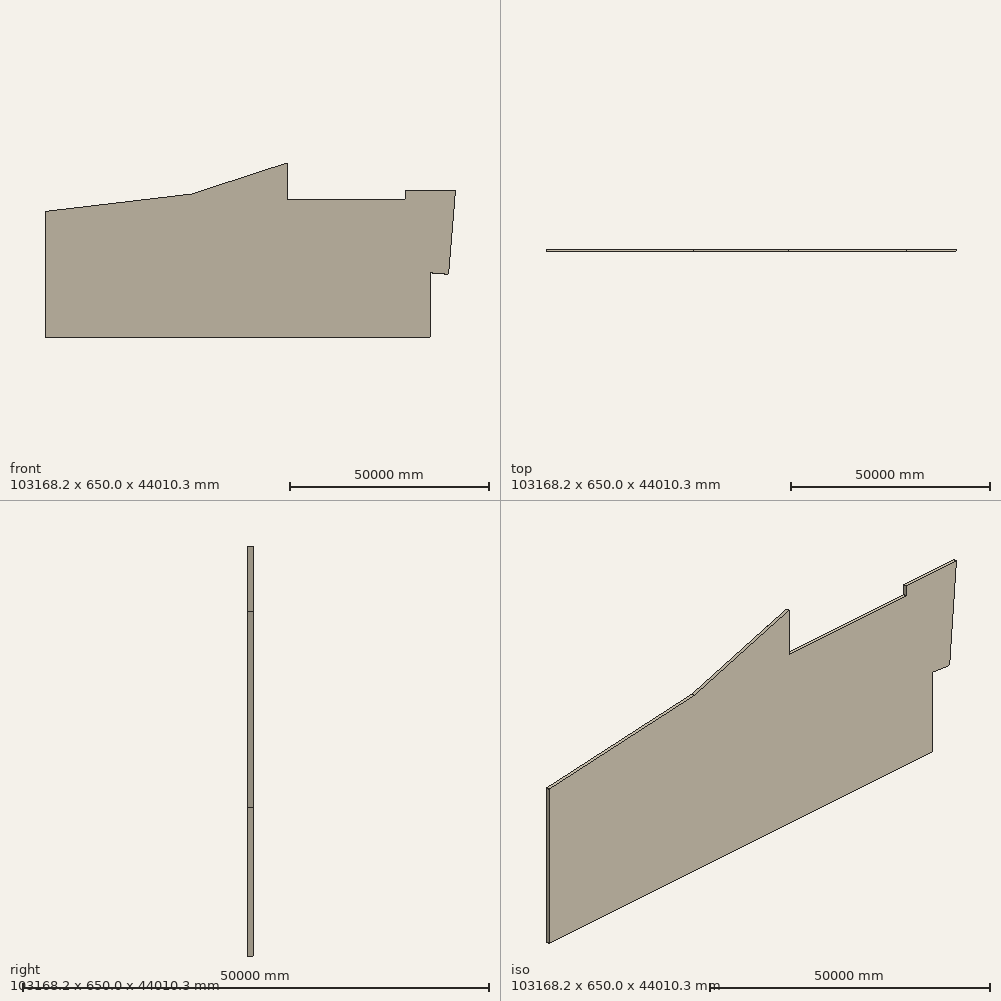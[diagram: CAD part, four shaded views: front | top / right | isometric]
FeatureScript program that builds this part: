
annotation { "Feature Type Name" : "Feature", "Feature Type Description" : "" }
export const myFeature = defineFeature(function(context is Context, id is Id, definition is map)
    precondition{}
    {
        {
            var Q0;
            Q0=qCreatedBy(makeId("Front.planeOp"),FACE);
            var sketch = newSketch(context, id + "F0", { "sketchPlane" : qUnion([Q0])});
            skLineSegment(sketch, "E0", {"start": v(0, 31823) * mm, "end": v(0, 0) * mm});
            skLineSegment(sketch, "E1", {"start": v(0, 0) * mm, "end": v(96994, 0) * mm});
            skLineSegment(sketch, "E2", {"start": v(0, 31823) * mm, "end": v(36871, 36212.16) * mm});
            skLineSegment(sketch, "E3", {"start": v(36871, 36212.16) * mm, "end": v(60811, 44010.33) * mm});
            skLineSegment(sketch, "E4", {"start": v(96994, 0) * mm, "end": v(96994, 16380) * mm});
            skPoint(sketch, "E5.end.orphan", {"position": v(65379, 52169.09) * mm});
            skPoint(sketch, "E6.end.orphan", {"position": v(91413.67, 52169.09) * mm});
            skLineSegment(sketch, "E7", {"start": v(60811, 44010.33) * mm, "end": v(60811, 34845.33) * mm});
            skLineSegment(sketch, "E8", {"start": v(60811, 34845.33) * mm, "end": v(90501, 34845.33) * mm});
            skLineSegment(sketch, "E9", {"start": v(96994, 16380) * mm, "end": v(101428, 16012.2) * mm});
            skLineSegment(sketch, "E10", {"start": v(101428, 16012.2) * mm, "end": v(103168.2, 36991.2) * mm});
            skLineSegment(sketch, "E11", {"start": v(103168.2, 36991.2) * mm, "end": v(90501, 36991.2) * mm});
            skLineSegment(sketch, "E12", {"start": v(90501, 34845.33) * mm, "end": v(90501, 36991.2) * mm});
            skSolve(sketch);
        }
        {
            var Q0;
            Q0=qSketchRegion(id+"F0",true);
            extrude(context, id + "F1", {"entities" : qUnion([Q0]), "depth" : 650 * mm});
        }
    });
